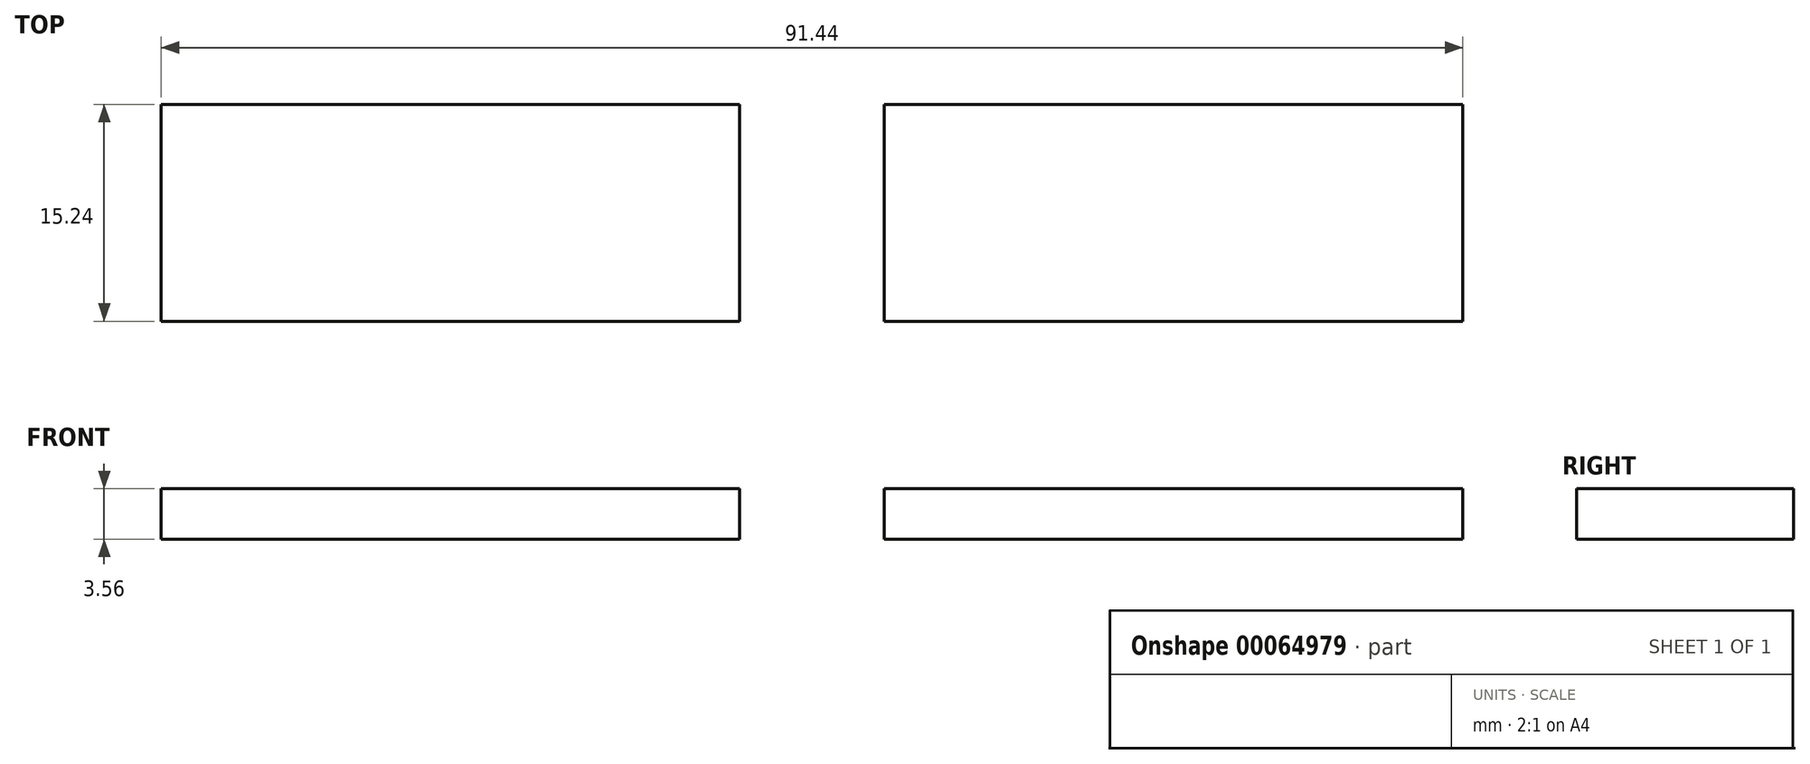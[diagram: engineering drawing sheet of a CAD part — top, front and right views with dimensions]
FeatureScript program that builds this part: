
annotation { "Feature Type Name" : "Feature", "Feature Type Description" : "" }
export const myFeature = defineFeature(function(context is Context, id is Id, definition is map)
    precondition{}
    {
        {
            var Q0;
            Q0=qCreatedBy(makeId("Top.planeOp"),FACE);
            var sketch = newSketch(context, id + "F0", { "sketchPlane" : qUnion([Q0])});
            skLineSegment(sketch, "E0.bottom", {"start": v(0, 0) * mm, "end": v(40.64, 0) * mm});
            skLineSegment(sketch, "E0.top", {"start": v(0, 15.24) * mm, "end": v(40.64, 15.24) * mm});
            skLineSegment(sketch, "E0.left", {"start": v(0, 0) * mm, "end": v(0, 15.24) * mm});
            skLineSegment(sketch, "E0.right", {"start": v(40.64, 0) * mm, "end": v(40.64, 15.24) * mm});
            skLineSegment(sketch, "E1", {"start": v(-5.08, 25.98) * mm, "end": v(-5.08, -26.45) * mm, "construction": true});
            skLineSegment(sketch, "E2.MirrorCS", {"start": v(-10.16, 15.24) * mm, "end": v(-50.8, 15.24) * mm});
            skLineSegment(sketch, "E3.MirrorCS", {"start": v(-10.16, 0) * mm, "end": v(-10.16, 15.24) * mm});
            skLineSegment(sketch, "E4.MirrorCS", {"start": v(-10.16, 0) * mm, "end": v(-50.8, 0) * mm});
            skLineSegment(sketch, "E5.MirrorCS", {"start": v(-50.8, 0) * mm, "end": v(-50.8, 15.24) * mm});
            skSolve(sketch);
        }
        {
            var Q0;
            Q0 = qSketchRegion(id + "F0", true);
            extrude(context, id + "F1", {"entities" : qUnion([Q0]), "depth" : 3.56 * mm});
        }
    });
